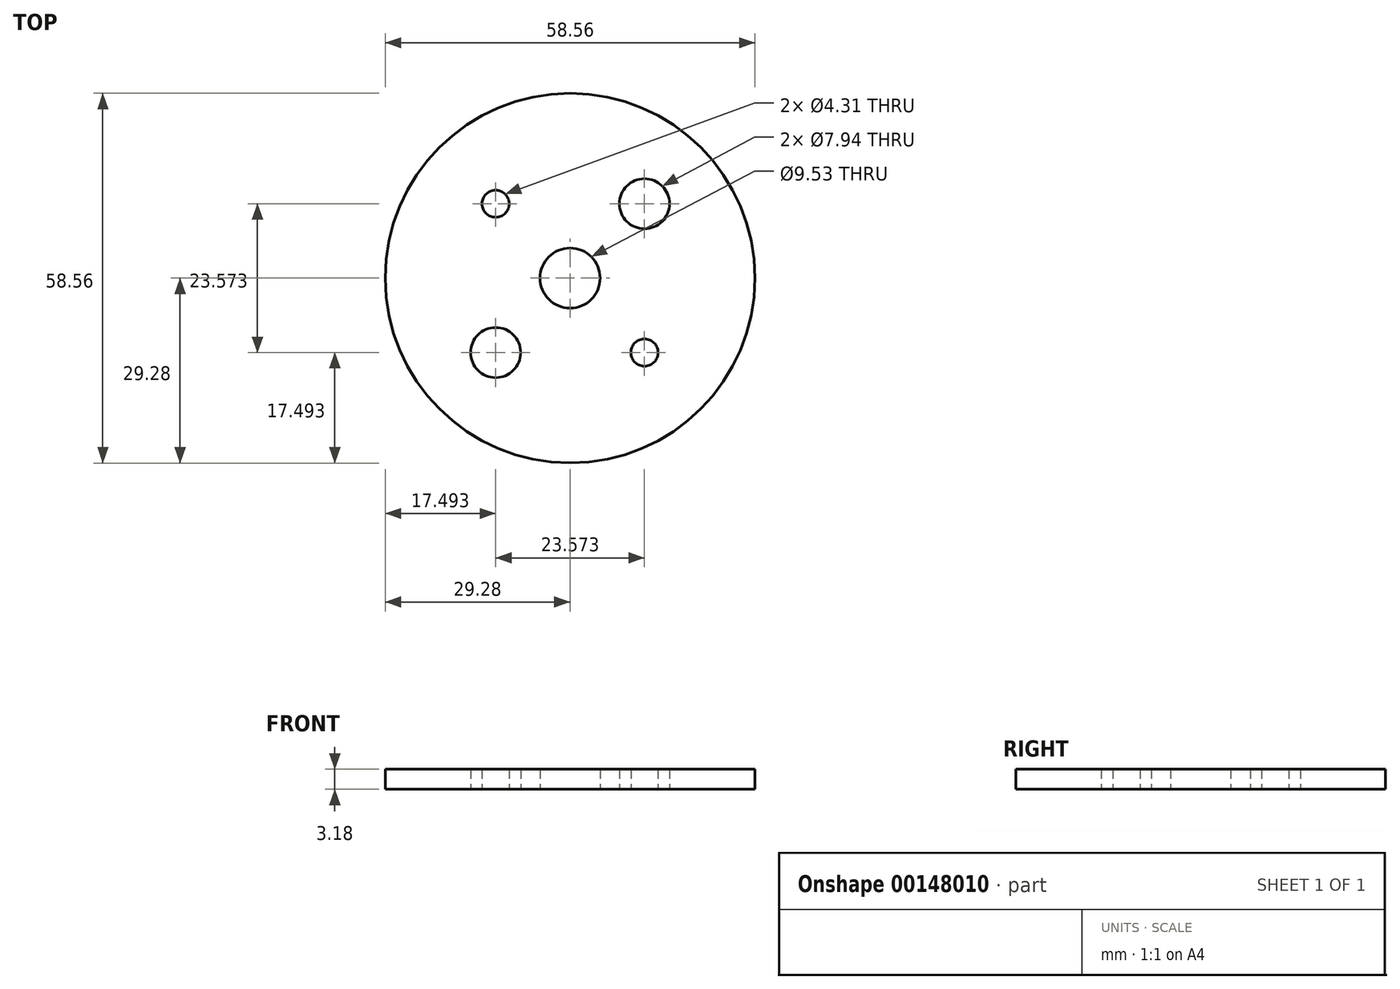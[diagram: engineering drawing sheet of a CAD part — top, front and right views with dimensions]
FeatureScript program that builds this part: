
annotation { "Feature Type Name" : "Feature", "Feature Type Description" : "" }
export const myFeature = defineFeature(function(context is Context, id is Id, definition is map)
    precondition{}
    {
        {
            var Q0;
            Q0=qCreatedBy(makeId("Top.planeOp"),FACE);
            var sketch = newSketch(context, id + "F0", { "sketchPlane" : qUnion([Q0])});
            skCircle(sketch, "E0", {"center": v(0, 0) * mm, "radius": 29.28 * mm});
            skCircle(sketch, "E1", {"center": v(0, 0) * mm, "radius": 4.76 * mm});
            skLineSegment(sketch, "E2.bottom", {"start": v(-11.79, 11.79) * mm, "end": v(11.79, 11.79) * mm, "construction": true});
            skLineSegment(sketch, "E2.top", {"start": v(-11.79, -11.79) * mm, "end": v(11.79, -11.79) * mm, "construction": true});
            skLineSegment(sketch, "E2.left", {"start": v(-11.79, 11.79) * mm, "end": v(-11.79, -11.79) * mm, "construction": true});
            skLineSegment(sketch, "E2.right", {"start": v(11.79, 11.79) * mm, "end": v(11.79, -11.79) * mm, "construction": true});
            skCircle(sketch, "E3", {"center": v(11.79, 11.79) * mm, "radius": 2.15 * mm, "construction": true});
            skCircle(sketch, "E4", {"center": v(-11.79, 11.79) * mm, "radius": 2.15 * mm});
            skCircle(sketch, "E5", {"center": v(-11.79, -11.79) * mm, "radius": 2.15 * mm, "construction": true});
            skCircle(sketch, "E6", {"center": v(11.79, -11.79) * mm, "radius": 2.15 * mm});
            skCircle(sketch, "E7", {"center": v(-11.79, -11.79) * mm, "radius": 3.97 * mm});
            skCircle(sketch, "E8", {"center": v(11.79, 11.79) * mm, "radius": 3.97 * mm});
            skSolve(sketch);
        }
        {
            var Q0;
            Q0=qSketchRegion(id+"F0",true);
            extrude(context, id + "F1", {"entities" : qUnion([Q0]), "depth" : 3.17 * mm});
        }
    });
